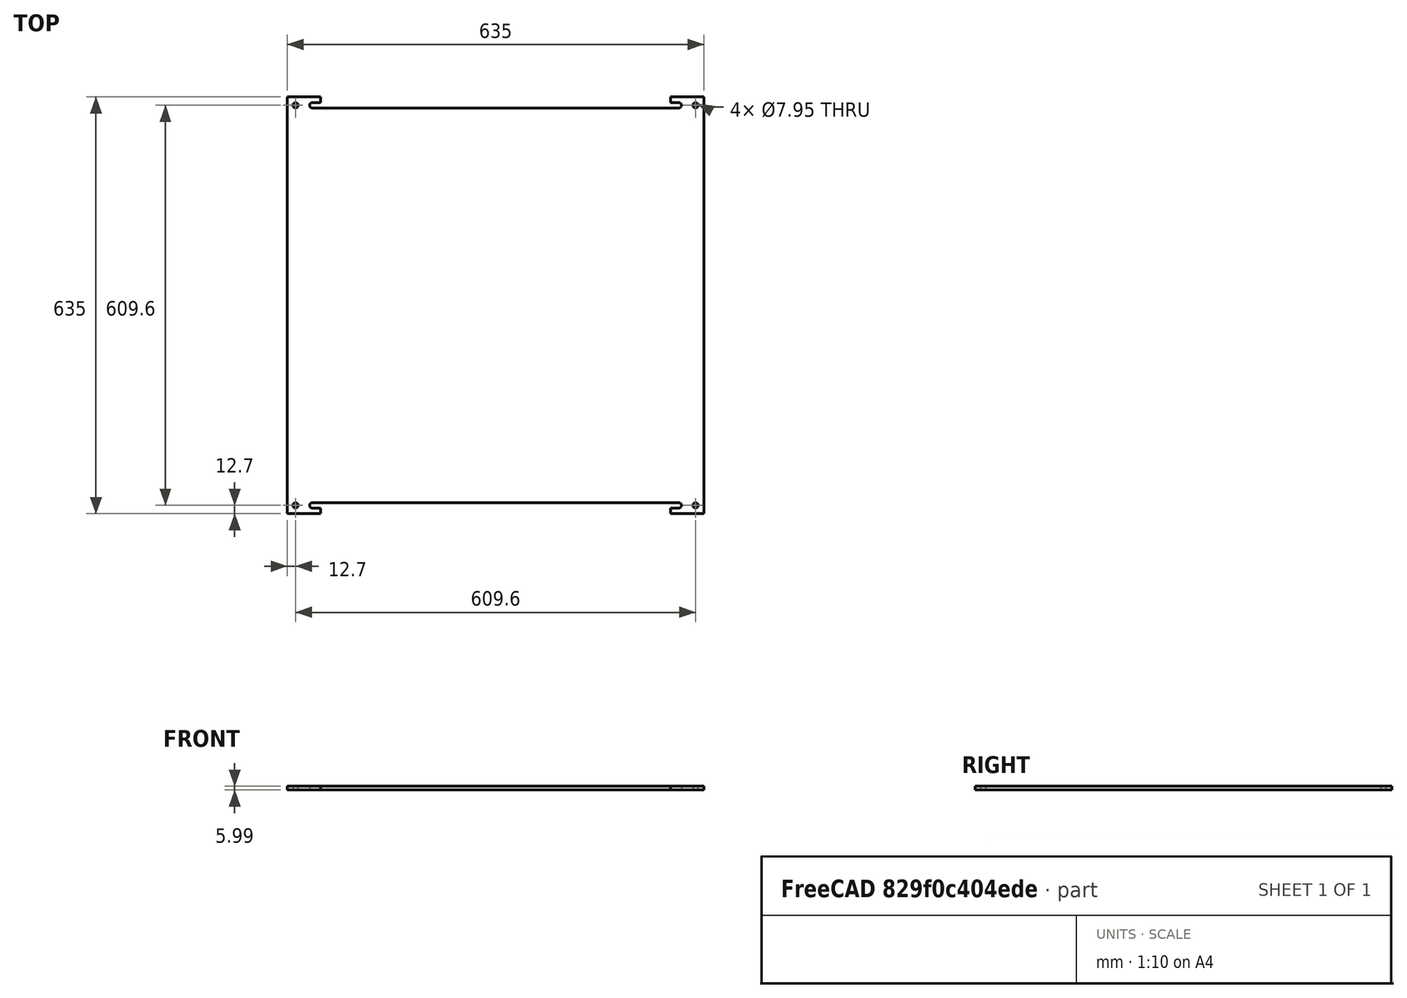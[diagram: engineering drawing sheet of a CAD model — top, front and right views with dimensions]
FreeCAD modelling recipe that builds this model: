
FCSTD DOCUMENT  (FreeCAD 0.19R24267 (Git))
Label: Inv2-P13
License: All rights reserved
LicenseURL: http://en.wikipedia.org/wiki/All_rights_reserved
objects: TechDraw::DrawViewDimension×10, TechDraw::DrawViewAnnotation×3, TechDraw::DrawProjGroupItem×2, TechDraw::DrawHatch×2, Sketcher::SketchObject×1, Part::Extrusion×1, TechDraw::DrawSVGTemplate×1, TechDraw::DrawProjGroup×1, TechDraw::DrawPage×1
note: 2 computed .brp shape members not serialized (recipe doc carries the construction recipe); baked Part::Feature solids carry a one-line shape summary decoded from their .brp

FEATURE [Sketcher::SketchObject] Sketch
  FullyConstrained = false
  sketch-geometry (39):
    g0: LineSegment StartX=0 StartY=0 StartZ=0 EndX=0 EndY=-635 EndZ=0
    g1: LineSegment StartX=0 StartY=-635 StartZ=0 EndX=50.8 EndY=-635 EndZ=0
    g2: LineSegment StartX=0 StartY=0 StartZ=0 EndX=50.8 EndY=0 EndZ=0
    g3: LineSegment StartX=50.8 StartY=0 StartZ=0 EndX=50.8 EndY=-8.7249 EndZ=0
    g4: LineSegment StartX=50.8 StartY=-8.7249 StartZ=0 EndX=38.1 EndY=-8.7249 EndZ=0
    g5: LineSegment StartX=38.1 StartY=-16.6751 StartZ=0 EndX=596.9 EndY=-16.6751 EndZ=0
    g6: LineSegment StartX=38.1 StartY=-8.7249 StartZ=0 EndX=38.1 EndY=-16.6751 EndZ=0
    g7: Circle CenterX=12.7 CenterY=-12.7 CenterZ=0 NormalX=0 NormalY=0 NormalZ=1 AngleXU=0 Radius=3.9751
    g8: ArcOfCircle CenterX=38.1 CenterY=-12.7 CenterZ=0 NormalX=0 NormalY=0 NormalZ=1 AngleXU=0 Radius=3.9751 StartAngle=1.5708 EndAngle=4.71239
    g9: LineSegment StartX=50.8 StartY=-635 StartZ=0 EndX=50.8 EndY=-626.275 EndZ=0
    g10: LineSegment StartX=50.8 StartY=-626.275 StartZ=0 EndX=38.1 EndY=-626.275 EndZ=0
    g11: LineSegment StartX=38.1 StartY=-618.325 StartZ=0 EndX=596.9 EndY=-618.325 EndZ=0
    g12: LineSegment StartX=38.1 StartY=-626.275 StartZ=0 EndX=38.1 EndY=-618.325 EndZ=0
    g13: ArcOfCircle CenterX=38.1 CenterY=-622.3 CenterZ=0 NormalX=0 NormalY=0 NormalZ=1 AngleXU=0 Radius=3.9751 StartAngle=1.5708 EndAngle=4.71239
    g14: Circle CenterX=12.7 CenterY=-622.3 CenterZ=0 NormalX=0 NormalY=0 NormalZ=1 AngleXU=0 Radius=3.9751
    g15: LineSegment StartX=38.1 StartY=-12.7 StartZ=0 EndX=0 EndY=-12.7 EndZ=0
    g16: LineSegment StartX=12.7 StartY=-12.7 StartZ=0 EndX=0 EndY=-12.7 EndZ=0
    g17: LineSegment StartX=24.8556 StartY=-12.7 StartZ=0 EndX=24.8556 EndY=0 EndZ=0
    g18: LineSegment StartX=0 StartY=-622.3 StartZ=0 EndX=12.7 EndY=-622.3 EndZ=0
    g19: LineSegment StartX=0 StartY=-622.3 StartZ=0 EndX=38.1 EndY=-622.3 EndZ=0
    g20: LineSegment StartX=23.3926 StartY=-622.3 StartZ=0 EndX=23.3926 EndY=-635 EndZ=0
    g21: LineSegment StartX=584.2 StartY=-8.7249 StartZ=0 EndX=596.9 EndY=-8.7249 EndZ=0
    g22: LineSegment StartX=584.2 StartY=-8.7249 StartZ=0 EndX=584.2 EndY=0 EndZ=0
    g23: LineSegment StartX=584.2 StartY=0 StartZ=0 EndX=635 EndY=0 EndZ=0
    g24: LineSegment StartX=635 StartY=0 StartZ=0 EndX=635 EndY=-635 EndZ=0
    g25: Circle CenterX=622.3 CenterY=-12.7 CenterZ=0 NormalX=0 NormalY=0 NormalZ=1 AngleXU=0 Radius=3.9751
    g26: LineSegment StartX=622.3 StartY=-12.7 StartZ=0 EndX=635 EndY=-12.7 EndZ=0
    g27: LineSegment StartX=635 StartY=-635 StartZ=0 EndX=584.2 EndY=-635 EndZ=0
    g28: LineSegment StartX=584.2 StartY=-635 StartZ=0 EndX=584.2 EndY=-626.275 EndZ=0
    g29: LineSegment StartX=584.2 StartY=-626.275 StartZ=0 EndX=596.9 EndY=-626.275 EndZ=0
    g30: LineSegment StartX=596.9 StartY=-626.275 StartZ=0 EndX=596.9 EndY=-618.325 EndZ=0
    g31: ArcOfCircle CenterX=596.9 CenterY=-622.3 CenterZ=0 NormalX=0 NormalY=0 NormalZ=1 AngleXU=0 Radius=3.9751 StartAngle=4.71239 EndAngle=7.85398
    g32: Circle CenterX=622.3 CenterY=-622.3 CenterZ=0 NormalX=0 NormalY=0 NormalZ=1 AngleXU=0 Radius=3.9751
    g33: LineSegment StartX=610.666 StartY=-622.3 StartZ=0 EndX=610.666 EndY=-635 EndZ=0
    g34: LineSegment StartX=622.3 StartY=-622.3 StartZ=0 EndX=635 EndY=-622.3 EndZ=0
    g35: LineSegment StartX=596.9 StartY=-622.3 StartZ=0 EndX=635 EndY=-622.3 EndZ=0
    g36: LineSegment StartX=596.9 StartY=-8.7249 StartZ=0 EndX=596.9 EndY=-16.6751 EndZ=0
    g37: LineSegment StartX=596.9 StartY=-12.7 StartZ=0 EndX=635 EndY=-12.7 EndZ=0
    g38: ArcOfCircle CenterX=596.9 CenterY=-12.7 CenterZ=0 NormalX=0 NormalY=0 NormalZ=1 AngleXU=0 Radius=3.9751 StartAngle=4.71239 EndAngle=7.85398
  constraints (114):
    c: Coincident(g0,g-1)
    c: PointOnObject(g0,g-2)
    c: Coincident(g1,g0)
    c: Horizontal(g1)
    c: Distance(g0) = 635
    c: Coincident(g2,g0)
    c: PointOnObject(g2,g-1)
    c: Coincident(g3,g2)
    c: Vertical(g3)
    c: Coincident(g4,g3)
    c: Horizontal(g4)
    c: Horizontal(g5)
    c: Coincident(g6,g4)
    c: Coincident(g6,g5)
    c: Vertical(g6)
    c: Distance(g2) = 50.8
    c: Diameter(g7) = 7.9502
    c: PointOnObject(g8,g6)
    c: Coincident(g8,g4)
    c: Coincident(g8,g5)
    c: Equal(g8,g7)
    c: Equal(g1,g2)
    c: Coincident(g9,g1)
    c: Vertical(g9)
    c: Coincident(g10,g9)
    c: Horizontal(g10)
    c: Horizontal(g11)
    c: Coincident(g12,g10)
    c: Coincident(g12,g11)
    c: Vertical(g12)
    c: PointOnObject(g13,g12)
    c: Coincident(g13,g11)
    c: Coincident(g13,g10)
    c: Coincident(g15,g8)
    c: PointOnObject(g15,g0)
    c: Horizontal(g15)
    c: Coincident(g16,g7)
    c: Distance(g15) = 38.1
    c: PointOnObject(g17,g15)
    c: PointOnObject(g17,g2)
    c: Vertical(g17)
    c: Distance(g17) = 12.7
    c: Equal(g16,g17)
    c: Horizontal(g16)
    c: Coincident(g16,g15)
    c: PointOnObject(g18,g0)
    c: Coincident(g18,g14)
    c: Coincident(g19,g18)
    c: Coincident(g19,g13)
    c: Horizontal(g19)
    c: PointOnObject(g20,g19)
    c: PointOnObject(g20,g1)
    c: Vertical(g20)
    c: Equal(g7,g14)
    c: Equal(g13,g7)
    c: Equal(g19,g15)
    c: Equal(g20,g17)
    c: Equal(g18,g17)
    c: Horizontal(g18)
    c: Horizontal(g21)
    c: Coincident(g22,g21)
    c: PointOnObject(g22,g-1)
    c: Vertical(g22)
    c: Coincident(g23,g22)
    c: PointOnObject(g23,g-1)
    c: Coincident(g24,g23)
    c: Vertical(g24)
    c: Equal(g7,g25)
    c: Equal(g23,g2)
    c: PointOnObject(g26,g24)
    c: Coincident(g26,g25)
    c: Equal(g26,g17)
    c: Horizontal(g26)
    c: Distance(g0,g24) = 635
    c: Coincident(g27,g24)
    c: Horizontal(g27)
    c: Equal(g27,g2)
    c: Coincident(g28,g27)
    c: Vertical(g28)
    c: Horizontal(g29)
    c: Coincident(g29,g28)
    c: Coincident(g30,g29)
    c: Coincident(g30,g11)
    c: Vertical(g30)
    c: PointOnObject(g31,g30)
    c: Coincident(g31,g11)
    c: Coincident(g31,g29)
    c: PointOnObject(g34,g24)
    c: Equal(g32,g7)
    c: PointOnObject(g33,g27)
    c: Vertical(g33)
    c: Equal(g33,g17)
    c: Equal(g7,g31)
    c: Coincident(g34,g32)
    c: Equal(g34,g17)
    c: Coincident(g35,g31)
    c: PointOnObject(g35,g24)
    c: Horizontal(g35)
    c: Equal(g35,g15)
    c: PointOnObject(g32,g35)
    c: Horizontal(g34)
    c: PointOnObject(g33,g35)
    c: Coincident(g36,g21)
    c: Coincident(g36,g5)
    c: Vertical(g36)
    c: PointOnObject(g37,g24)
    c: Horizontal(g37)
    c: Equal(g37,g15)
    c: PointOnObject(g25,g37)
    c: Coincident(g38,g37)
    c: Coincident(g38,g21)
    c: Coincident(g38,g5)
    c: Equal(g38,g7)
    c: PointOnObject(g38,g36)
FEATURE [Part::Extrusion] Extrude
  Base = -> Sketch
  Dir = (0,0,1)
  DirMode = 2
  FaceMakerClass = Part::FaceMakerBullseye
  LengthFwd = 5.9944
  LengthRev = 0
  Solid = true
  Symmetric = false
FEATURE [TechDraw::DrawSVGTemplate] Template
  Height = 215.9
  Orientation = 1
  Width = 279.4
FEATURE [TechDraw::DrawProjGroupItem] ProjItem  label="Front"
  CoarseView = false
  Direction = (0,0,1)
  Focus = 100
  HardHidden = false
  IsoCount = 0
  IsoHidden = false
  IsoVisible = false
  LockPosition = true
  Perspective = false
  Rotation = 0
  RotationVector = (-1,0,0)
  Scale = 0.2
  ScaleType = 2
  SeamHidden = false
  SeamVisible = true
  SmoothHidden = false
  SmoothVisible = true
  Source = -> [Extrude]
  Type = 0
  X = 0
  XDirection = (-1,0,0)
  Y = 0
FEATURE [TechDraw::DrawProjGroupItem] ProjItem001  label="Left"
  CoarseView = false
  Direction = (1,0,1e-16)
  Focus = 100
  HardHidden = false
  IsoCount = 0
  IsoHidden = false
  IsoVisible = false
  LockPosition = false
  Perspective = false
  Rotation = 0
  RotationVector = (1,0,0)
  ScaleType = 2
  SeamHidden = false
  SeamVisible = true
  SmoothHidden = false
  SmoothVisible = true
  Source = -> [Extrude]
  Type = 1
  X = 109.723
  XDirection = (-1e-16,0,1)
  Y = 0
FEATURE [TechDraw::DrawProjGroup] ProjGroup
  Anchor = -> ProjItem
  AutoDistribute = true
  LockPosition = false
  ProjectionType = 0
  Rotation = 0
  Scale = 0.2
  ScaleType = 2
  Source = -> [Extrude]
  Views = -> [ProjItem,ProjItem001]
  X = 121.135
  Y = 100.927
  spacingX = 15.0114
  spacingY = 15.0114
FEATURE [TechDraw::DrawHatch] Hatch  label="HatchF0"
  HatchPattern = <path>
  Source = -> ProjItem [Face0]
FEATURE [TechDraw::DrawHatch] Hatch001  label="Hatch001F0"
  HatchPattern = <path>
  Source = -> ProjItem001 [Face0]
FEATURE [TechDraw::DrawViewDimension] Dimension
  Arbitrary = false
  ArbitraryTolerances = false
  EqualTolerance = true
  FormatSpec = %.3f
  FormatSpecOverTolerance = %+.3f
  FormatSpecUnderTolerance = %+.3f
  Inverted = false
  LockPosition = false
  MeasureType = 1
  OverTolerance = 0
  References2D = -> [ProjItem]
  Rotation = 0
  ScaleType = 0
  TheoreticalExact = false
  Type = 2
  UnderTolerance = 0
  X = 78.0743
  Y = 0
FEATURE [TechDraw::DrawViewDimension] Dimension001
  Arbitrary = false
  ArbitraryTolerances = false
  EqualTolerance = true
  FormatSpec = %.3f
  FormatSpecOverTolerance = %+.3f
  FormatSpecUnderTolerance = %+.3f
  Inverted = false
  LockPosition = false
  MeasureType = 1
  OverTolerance = 0
  References2D = -> [ProjItem]
  Rotation = 0
  ScaleType = 0
  TheoreticalExact = false
  Type = 1
  UnderTolerance = 0
  X = 1.53513
  Y = -66.9856
FEATURE [TechDraw::DrawViewDimension] Dimension002
  Arbitrary = false
  ArbitraryTolerances = false
  EqualTolerance = true
  FormatSpec = %.3f
  FormatSpecOverTolerance = %+.3f
  FormatSpecUnderTolerance = %+.3f
  Inverted = false
  LockPosition = false
  MeasureType = 1
  OverTolerance = 0
  References2D = -> [ProjItem001]
  Rotation = 0
  ScaleType = 0
  TheoreticalExact = false
  Type = 1
  UnderTolerance = 0
  X = 15.2734
  Y = 43.3607
FEATURE [TechDraw::DrawViewDimension] Dimension003
  Arbitrary = false
  ArbitraryTolerances = false
  EqualTolerance = true
  FormatSpec = ⌀%.3f
  FormatSpecOverTolerance = %+.3f
  FormatSpecUnderTolerance = %+.3f
  Inverted = false
  LockPosition = false
  MeasureType = 1
  OverTolerance = 0
  References2D = -> [ProjItem]
  Rotation = 0
  ScaleType = 0
  TheoreticalExact = false
  Type = 5
  UnderTolerance = 0
  X = -75.5328
  Y = 50.363
FEATURE [TechDraw::DrawViewDimension] Dimension004
  Arbitrary = false
  ArbitraryTolerances = false
  EqualTolerance = true
  FormatSpec = ⌀%.3f
  FormatSpecOverTolerance = %+.3f
  FormatSpecUnderTolerance = %+.3f
  Inverted = false
  LockPosition = false
  MeasureType = 1
  OverTolerance = 0
  References2D = -> [ProjItem]
  Rotation = 0
  ScaleType = 0
  TheoreticalExact = false
  Type = 5
  UnderTolerance = 0
  X = -70.365
  Y = 44.5565
FEATURE [TechDraw::DrawViewDimension] Dimension005
  Arbitrary = false
  ArbitraryTolerances = false
  EqualTolerance = true
  FormatSpec = %.3f
  FormatSpecOverTolerance = %+.3f
  FormatSpecUnderTolerance = %+.3f
  Inverted = false
  LockPosition = false
  MeasureType = 1
  OverTolerance = 0
  References2D = -> [ProjItem]
  Rotation = 0
  ScaleType = 0
  TheoreticalExact = false
  Type = 1
  UnderTolerance = 0
  X = -20.592
  Y = 78.7594
FEATURE [TechDraw::DrawViewDimension] Dimension006
  Arbitrary = false
  ArbitraryTolerances = false
  EqualTolerance = true
  FormatSpec = %.3f
  FormatSpecOverTolerance = %+.3f
  FormatSpecUnderTolerance = %+.3f
  Inverted = false
  LockPosition = false
  MeasureType = 1
  OverTolerance = 0
  References2D = -> [ProjItem]
  Rotation = 0
  ScaleType = 0
  TheoreticalExact = false
  Type = 2
  UnderTolerance = 0
  X = -87.8233
  Y = 45.1899
FEATURE [TechDraw::DrawViewDimension] Dimension007
  Arbitrary = false
  ArbitraryTolerances = false
  EqualTolerance = true
  FormatSpec = %.3f
  FormatSpecOverTolerance = %+.3f
  FormatSpecUnderTolerance = %+.3f
  Inverted = false
  LockPosition = false
  MeasureType = 1
  OverTolerance = 0
  References2D = -> [ProjItem]
  Rotation = 0
  ScaleType = 0
  TheoreticalExact = false
  Type = 1
  UnderTolerance = 0
  X = -45.6686
  Y = 84.9769
FEATURE [TechDraw::DrawViewDimension] Dimension008
  Arbitrary = false
  ArbitraryTolerances = false
  EqualTolerance = true
  FormatSpec = %.3f
  FormatSpecOverTolerance = %+.3f
  FormatSpecUnderTolerance = %+.3f
  Inverted = false
  LockPosition = false
  MeasureType = 1
  OverTolerance = 0
  References2D = -> [ProjItem]
  Rotation = 0
  ScaleType = 0
  TheoreticalExact = false
  Type = 1
  UnderTolerance = 0
  X = -32.867
  Y = 81.429
FEATURE [TechDraw::DrawViewDimension] Dimension009
  Arbitrary = false
  ArbitraryTolerances = false
  EqualTolerance = true
  FormatSpec = %.3f
  FormatSpecOverTolerance = %+.3f
  FormatSpecUnderTolerance = %+.3f
  Inverted = false
  LockPosition = false
  MeasureType = 1
  OverTolerance = 0
  References2D = -> [ProjItem]
  Rotation = 0
  ScaleType = 0
  TheoreticalExact = false
  Type = 2
  UnderTolerance = 0
  X = -49.6959
  Y = 39.6042
FEATURE [TechDraw::DrawViewAnnotation] Annotation
  Font = osifont
  LineSpace = 80
  LockPosition = false
  MaxWidth = -1
  Rotation = 0
  ScaleType = 0
  Text = Figure S2 (Inverted 2) | Panel 13 [top] | Quantity: 1
  TextSize = 5.0038
  TextStyle = 0
  X = 33.0122
  Y = 195.58
FEATURE [TechDraw::DrawViewAnnotation] Annotation002
  Font = osifont
  LineSpace = 80
  LockPosition = false
  MaxWidth = -1
  Rotation = 0
  ScaleType = 0
  Text = Units: Inches
  TextSize = 5.0038
  TextStyle = 0
  X = 259.08
  Y = 5.08
FEATURE [TechDraw::DrawViewAnnotation] Annotation003
  Font = osifont
  LineSpace = 80
  LockPosition = false
  MaxWidth = -1
  Rotation = 0
  ScaleType = 0
  Text = same each corner
  TextSize = 5.0038
  TextStyle = 0
  X = 100.471
  Y = 151.054
FEATURE [TechDraw::DrawPage] Page
  KeepUpdated = true
  NextBalloonIndex = 1
  ProjectionType = 0
  Template = -> Template
  Views = -> [ProjGroup,Dimension,Dimension001,Dimension002,Dimension003,Dimension004,Dimension005,Dimension006,Dimension007,Dimension008,Dimension009,Annotation,Annotation002,Annotation003]
note: 2 file-system paths scrubbed to <path> (originals preserved in the JSON sidecar)
